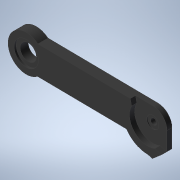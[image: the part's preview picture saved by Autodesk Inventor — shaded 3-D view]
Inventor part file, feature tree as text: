
AUTODESK INVENTOR PART (.ipt)
format: ipt  version: 2020.2 (Build 242310000, 310)  size: 230,912 bytes
history: native  units: mm
features: extrude x8, other x6, sketch x6, hole x2
ambient origin geometry x8: Origin, YZ Plane, XZ Plane, XY Plane, X Axis, Y Axis, Z Axis, Center Point
bodies: Body1 (feature_tree)
feature tree (22):
  other  "ソリッド1"
  sketch  "スケッチ1"
  extrude  "押し出し1"  Depth=5.0mm
  extrude  "押し出し2"  Depth=6.0mm
  hole  "穴1"  [1 undecoded]
  extrude  "押し出し3"  Depth=17.771543mm
  extrude  "押し出し4"  Depth=0.5mm
  hole  "穴2"  [1 undecoded]
  sketch  "スケッチ4"
  extrude  "押し出し5"  Depth=2.55mm TaperAngle=0.0deg
  extrude  "押し出し6"  Depth=5.0mm
  extrude  "押し出し7"  Depth=5.0mm TaperAngle=0.0deg
  extrude  "押し出し8"  Depth=10.0mm TaperAngle=0.0deg
  sketch  "スケッチ2"
  sketch  "スケッチ3"
  sketch  "スケッチ5"
  sketch  "スケッチ6"
  other  "断面エッジを投影1"
  other  "断面エッジを投影2"
  other  "断面エッジを投影3"
  other  "断面エッジを投影4"
  other  "断面エッジを投影5"
note: 2 required parameter values undecoded (feature->parameter linkage not recoverable at this tier; creation-order binding heuristic only, values carry confidence <= 0.55)
